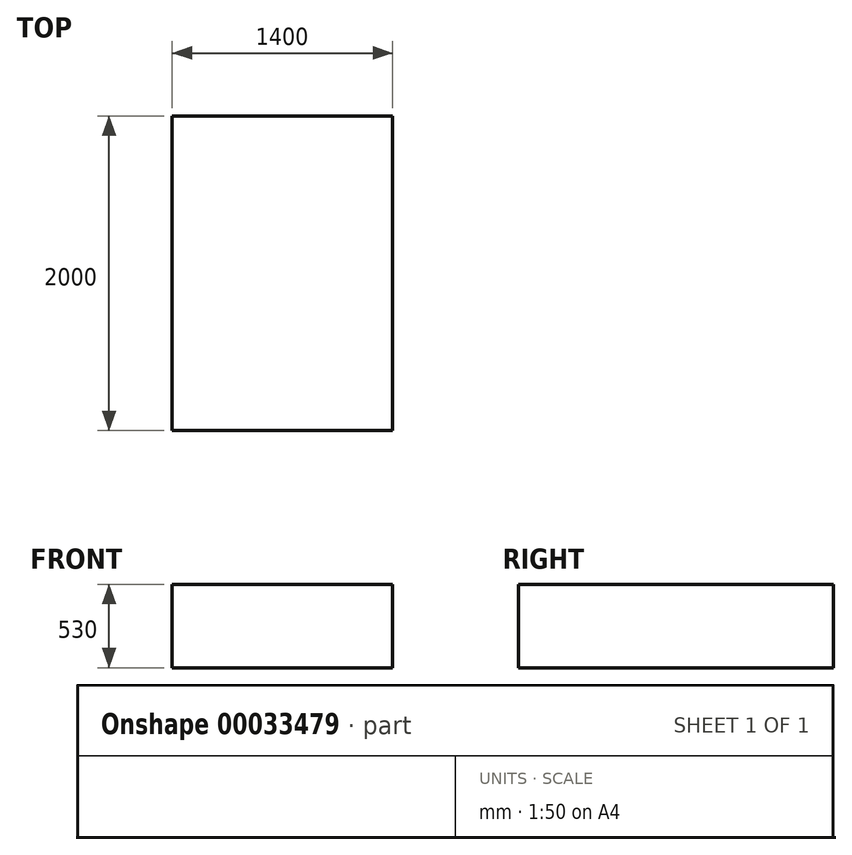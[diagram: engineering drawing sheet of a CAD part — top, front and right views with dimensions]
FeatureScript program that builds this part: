
annotation { "Feature Type Name" : "Feature", "Feature Type Description" : "" }
export const myFeature = defineFeature(function(context is Context, id is Id, definition is map)
    precondition{}
    {
        {
            var Q0;
            Q0=qCreatedBy(makeId("Top.planeOp"),FACE);
            var sketch = newSketch(context, id + "F0", { "sketchPlane" : qUnion([Q0])});
            skLineSegment(sketch, "E0.bottom", {"start": v(-702.05, 1153.95) * mm, "end": v(697.95, 1153.95) * mm});
            skLineSegment(sketch, "E0.top", {"start": v(-702.05, -846.05) * mm, "end": v(697.95, -846.05) * mm});
            skLineSegment(sketch, "E0.left", {"start": v(-702.05, 1153.95) * mm, "end": v(-702.05, -846.05) * mm});
            skLineSegment(sketch, "E0.right", {"start": v(697.95, 1153.95) * mm, "end": v(697.95, -846.05) * mm});
            skSolve(sketch);
        }
        {
            var Q0;
            Q0=makeQuery(id+"F0.imprint","IMPRINT",FACE,{"disambiguationData":[TD([[makeQuery(id+"F0.imprint","IMPRINT",EDGE,{"derivedFrom":sQuery(id+"F0.wireOp",EDGE,"E0.bottom")}),-1.0]])]});
            extrude(context, id + "F1", {"entities" : qUnion([Q0]), "depth" : 530 * mm});
        }
    });
